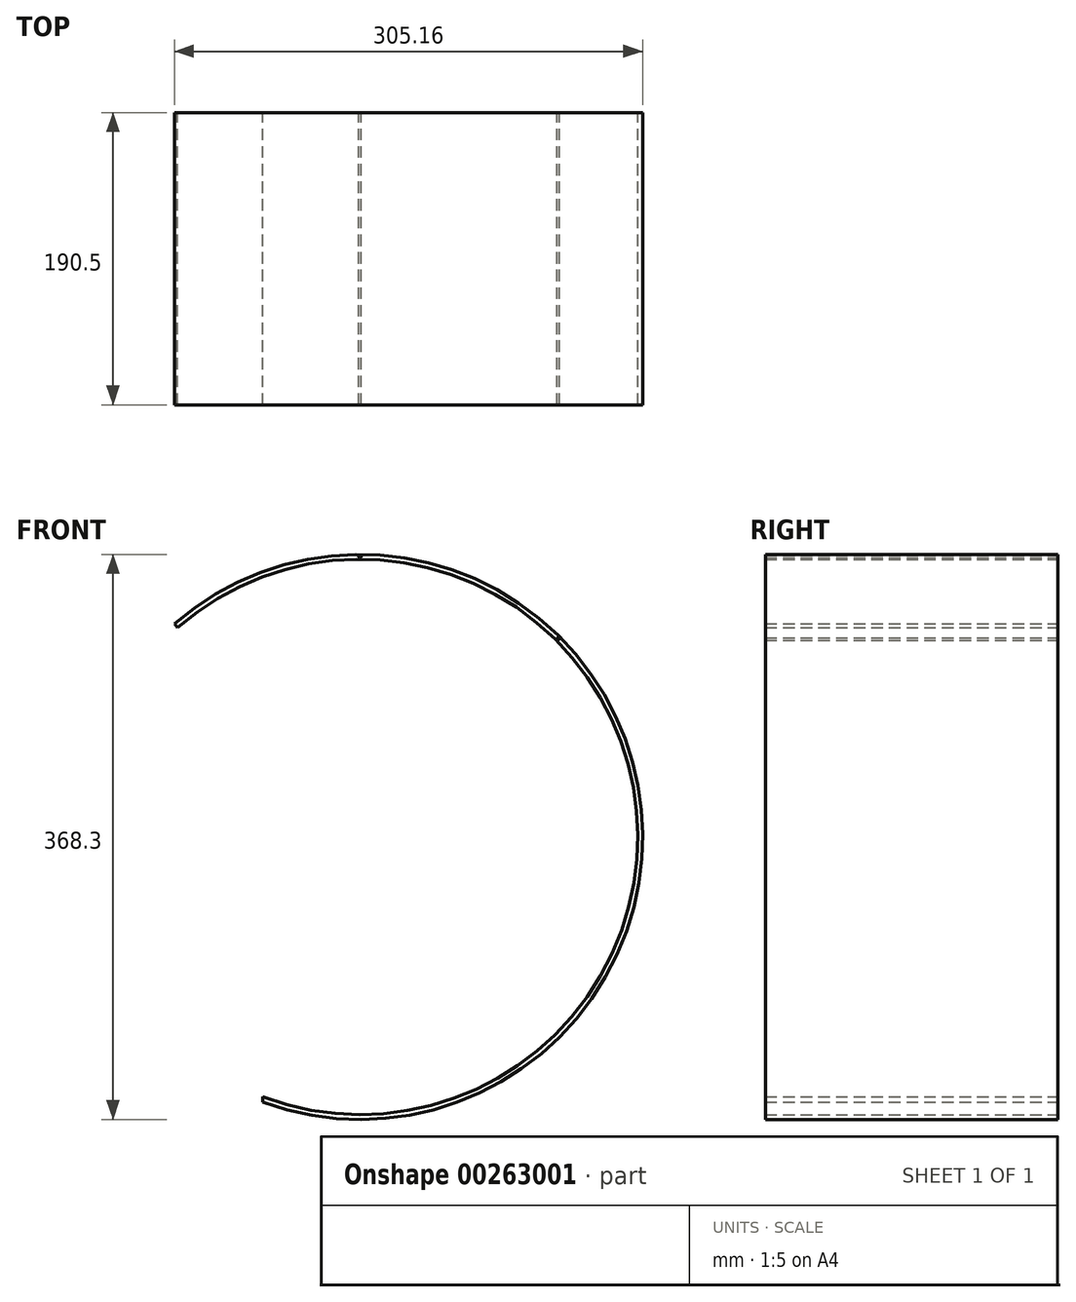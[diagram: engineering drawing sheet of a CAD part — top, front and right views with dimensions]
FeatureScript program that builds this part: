
annotation { "Feature Type Name" : "Feature", "Feature Type Description" : "" }
export const myFeature = defineFeature(function(context is Context, id is Id, definition is map)
    precondition{}
    {
        {
            var Q0;
            Q0=qCreatedBy(makeId("Front.planeOp"),FACE);
            var sketch = newSketch(context, id + "F0", { "sketchPlane" : qUnion([Q0])});
            skArc(sketch, "E0", {"start": v(-63.5, -169.47) * mm, "mid": v(178.08, 32.27) * mm, "end": v(-118.93, 136.41) * mm});
            skArc(sketch, "E1", {"start": v(-63.5, -172.86) * mm, "mid": v(181.1, 33.42) * mm, "end": v(-121.01, 138.8) * mm});
            skLineSegment(sketch, "E2", {"start": v(-118.93, 136.41) * mm, "end": v(-121.01, 138.8) * mm});
            skLineSegment(sketch, "E3", {"start": v(0, 180.98) * mm, "end": v(0, 184.15) * mm});
            skLineSegment(sketch, "E4", {"start": v(-63.5, -169.47) * mm, "end": v(-63.5, -172.86) * mm});
            skCircle(sketch, "E5", {"center": v(0, 182.56) * mm, "radius": 0.8 * mm});
            skCircle(sketch, "E6", {"center": v(129.1, 129.1) * mm, "radius": 0.8 * mm});
            skSolve(sketch);
        }
        {
            var Q0;
            Q0 = qSketchRegion(id + "F0", true);
            extrude(context, id + "F1", {"entities" : qUnion([Q0]), "depth" : 190.5 * mm});
        }
    });
